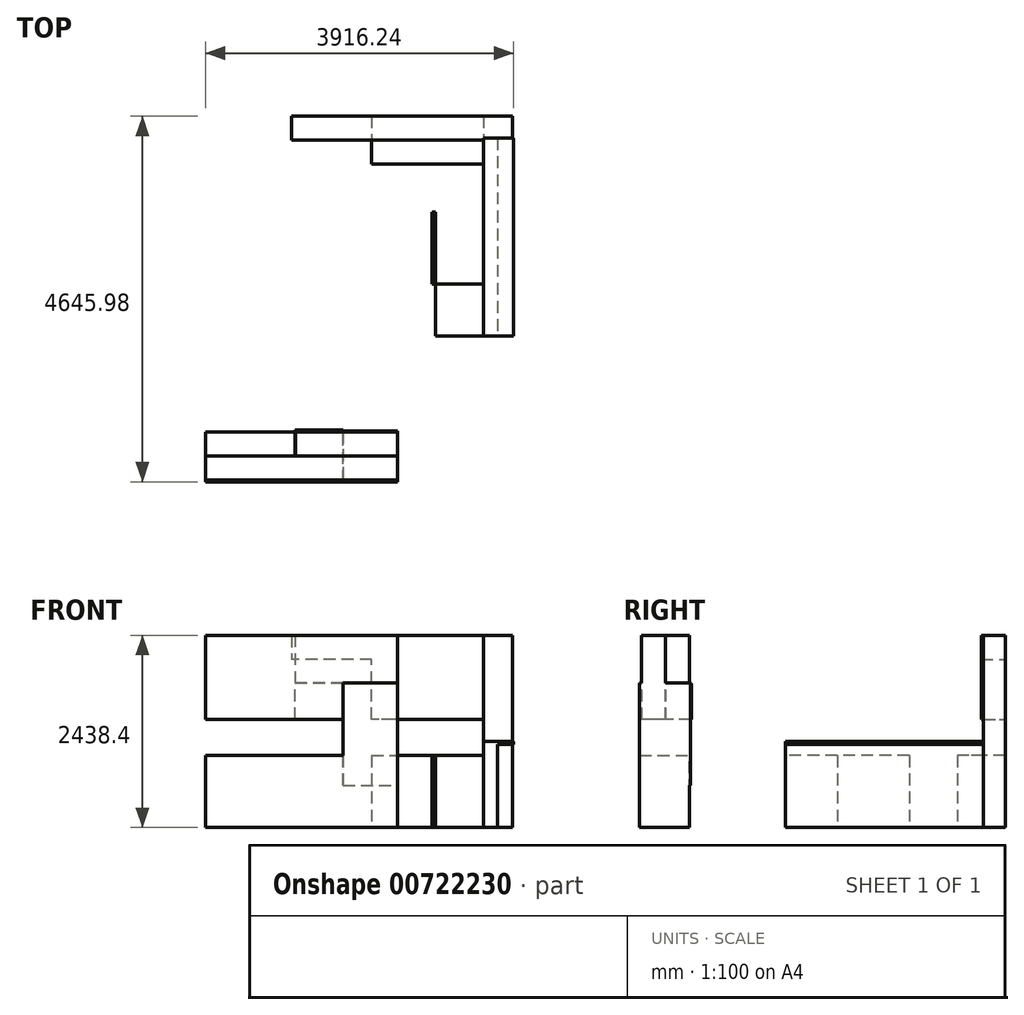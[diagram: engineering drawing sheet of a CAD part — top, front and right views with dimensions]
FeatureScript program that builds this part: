
annotation { "Feature Type Name" : "Feature", "Feature Type Description" : "" }
export const myFeature = defineFeature(function(context is Context, id is Id, definition is map)
    precondition{}
    {
        {
            var Q0;
            Q0=qCreatedBy(makeId("Top.planeOp"),FACE);
            var sketch = newSketch(context, id + "F0", { "sketchPlane" : qUnion([Q0])});
            skLineSegment(sketch, "E0.bottom", {"start": v(0, 0) * mm, "end": v(1422.4, 0) * mm});
            skLineSegment(sketch, "E0.top", {"start": v(0, -609.6) * mm, "end": v(1422.4, -609.6) * mm});
            skLineSegment(sketch, "E0.left", {"start": v(0, 0) * mm, "end": v(0, -609.6) * mm});
            skLineSegment(sketch, "E0.right", {"start": v(1422.4, 0) * mm, "end": v(1422.4, -609.6) * mm});
            skLineSegment(sketch, "E1.bottom", {"start": v(1422.4, -609.6) * mm, "end": v(812.8, -609.6) * mm});
            skLineSegment(sketch, "E1.top", {"start": v(1422.4, -2794) * mm, "end": v(812.8, -2794) * mm});
            skLineSegment(sketch, "E1.left", {"start": v(1422.4, -609.6) * mm, "end": v(1422.4, -2794) * mm});
            skLineSegment(sketch, "E1.right", {"start": v(812.8, -609.6) * mm, "end": v(812.8, -2794) * mm});
            skLineSegment(sketch, "E2.bottom", {"start": v(769.1, -1219.2) * mm, "end": v(1422.4, -1219.2) * mm});
            skLineSegment(sketch, "E2.top", {"start": v(769.1, -2133.6) * mm, "end": v(1422.4, -2133.6) * mm});
            skLineSegment(sketch, "E2.left", {"start": v(769.1, -1219.2) * mm, "end": v(769.1, -2133.6) * mm});
            skLineSegment(sketch, "E2.right", {"start": v(1422.4, -1219.2) * mm, "end": v(1422.4, -2133.6) * mm});
            skSolve(sketch);
        }
        {
            var Q0;
            Q0=makeQuery(id+"F0.imprint","IMPRINT",FACE,{"disambiguationData":[TD([[makeQuery(id+"F0.imprint","IMPRINT",EDGE,{"derivedFrom":sQuery(id+"F0.wireOp",EDGE,"E0.bottom")}),-1.0]])]});
            var Q1;
            {var subQ0=sQuery(id+"F0.wireOp",EDGE,"E1.bottom");Q1=makeQuery(id+"F0.imprint","IMPRINT",FACE,{"disambiguationData":[TD([[makeQuery(id+"F0.imprint","IMPRINT",EDGE,{"derivedFrom":subQ0}),1.0]])]});}
            var Q2;
            {var subQ5=sQuery(id+"F0.wireOp",EDGE,"E2.right");Q2=makeQuery(id+"F0.imprint","IMPRINT",FACE,{"disambiguationData":[TD([[makeQuery(id+"F0.imprint","IMPRINT",EDGE,{"derivedFrom":subQ5}),-1.0]])]});}
            var Q3;
            {var subQ5=sQuery(id+"F0.wireOp",EDGE,"E2.left");Q3=makeQuery(id+"F0.imprint","IMPRINT",FACE,{"disambiguationData":[TD([[makeQuery(id+"F0.imprint","IMPRINT",EDGE,{"derivedFrom":subQ5}),1.0]])]});}
            var Q4;
            {var subQ0=sQuery(id+"F0.wireOp",EDGE,"E1.top");Q4=makeQuery(id+"F0.imprint","IMPRINT",FACE,{"disambiguationData":[TD([[makeQuery(id+"F0.imprint","IMPRINT",EDGE,{"derivedFrom":subQ0}),-1.0]])]});}
            extrude(context, id + "F1", {"entities" : qUnion([Q0, Q1, Q2, Q3, Q4]), "depth" : 914.4 * mm, "offsetDistance" : 25.4 * mm});
        }
        {
            var Q0;
            Q0=makeQuery(id+"F1.opExtrude","SWEPT_FACE",FACE,{"disambiguationData":[OSD([sQuery(id+"F0.wireOp",EDGE,"E1.top")])]});
            var sketch = newSketch(context, id + "F2", { "sketchPlane" : qUnion([Q0])});
            skLineSegment(sketch, "E3.bottom", {"start": v(1422.4, 0) * mm, "end": v(1600.2, 0) * mm});
            skLineSegment(sketch, "E3.top", {"start": v(1422.4, 1092.2) * mm, "end": v(1600.2, 1092.2) * mm});
            skLineSegment(sketch, "E3.left", {"start": v(1422.4, 0) * mm, "end": v(1422.4, 1092.2) * mm});
            skLineSegment(sketch, "E3.right", {"start": v(1600.2, 0) * mm, "end": v(1600.2, 1092.2) * mm});
            skLineSegment(sketch, "E4.bottom", {"start": v(1600.2, 1092.2) * mm, "end": v(1803.4, 1092.2) * mm});
            skLineSegment(sketch, "E4.top", {"start": v(1600.2, 1054.1) * mm, "end": v(1803.4, 1054.1) * mm});
            skLineSegment(sketch, "E4.left", {"start": v(1600.2, 1092.2) * mm, "end": v(1600.2, 1054.1) * mm});
            skLineSegment(sketch, "E4.right", {"start": v(1803.4, 1092.2) * mm, "end": v(1803.4, 1054.1) * mm});
            skSolve(sketch);
        }
        {
            var Q0;
            {var subQ4=sQuery(id+"F2.wireOp",EDGE,"E3.bottom");Q0=makeQuery(id+"F2.imprint","IMPRINT",FACE,{"disambiguationData":[TD([[makeQuery(id+"F2.imprint","IMPRINT",EDGE,{"derivedFrom":subQ4}),1.0]])]});}
            var Q1;
            Q1=makeQuery(id+"F2.imprint","IMPRINT",FACE,{"disambiguationData":[TD([[makeQuery(id+"F2.imprint","IMPRINT",EDGE,{"derivedFrom":sQuery(id+"F2.wireOp",EDGE,"E4.bottom")}),-1.0]])]});
            extrude(context, id + "F3", {"entities" : qUnion([Q0, Q1]), "oppositeDirection" : true, "depth" : 2514.6 * mm, "offsetDistance" : 25.4 * mm});
        }
        {
            var Q0;
            Q0=makeQuery(id+"F1.opExtrude","CAP_FACE",FACE,{"disambiguationData":[OSD([sQuery(id+"F0.wireOp",EDGE,"E0.bottom"),sQuery(id+"F0.wireOp",EDGE,"E0.top"),sQuery(id+"F0.wireOp",EDGE,"E0.left"),sQuery(id+"F0.wireOp",EDGE,"E0.right"),sQuery(id+"F0.wireOp",EDGE,"E1.top"),sQuery(id+"F0.wireOp",EDGE,"E1.left"),sQuery(id+"F0.wireOp",EDGE,"E1.right"),sQuery(id+"F0.wireOp",EDGE,"E2.bottom"),sQuery(id+"F0.wireOp",EDGE,"E2.top"),sQuery(id+"F0.wireOp",EDGE,"E2.left"),sQuery(id+"F0.wireOp",EDGE,"E2.right")])],"isStart":true});
            var sketch = newSketch(context, id + "F4", { "sketchPlane" : qUnion([Q0])});
            skLineSegment(sketch, "E5.bottom", {"start": v(1422.4, 278.96) * mm, "end": v(1786.64, 278.96) * mm});
            skLineSegment(sketch, "E5.top", {"start": v(1422.4, 0) * mm, "end": v(1786.64, 0) * mm});
            skLineSegment(sketch, "E5.left", {"start": v(1422.4, 278.96) * mm, "end": v(1422.4, 0) * mm});
            skLineSegment(sketch, "E5.right", {"start": v(1786.64, 278.96) * mm, "end": v(1786.64, 0) * mm});
            skSolve(sketch);
        }
        {
            var Q0;
            Q0=makeQuery(id+"F4.imprint","IMPRINT",FACE,{"disambiguationData":[TD([[makeQuery(id+"F4.imprint","IMPRINT",EDGE,{"derivedFrom":sQuery(id+"F4.wireOp",EDGE,"E5.bottom")}),-1.0]])]});
            extrude(context, id + "F5", {"entities" : qUnion([Q0]), "operationType" : NewBodyOperationType.ADD, "oppositeDirection" : true, "depth" : 2438.4 * mm, "offsetDistance" : 25.4 * mm});
        }
        {
            var Q0;
            Q0=makeQuery(id+"F1.opExtrude","CAP_FACE",FACE,{"disambiguationData":[OSD([sQuery(id+"F0.wireOp",EDGE,"E0.bottom"),sQuery(id+"F0.wireOp",EDGE,"E0.top"),sQuery(id+"F0.wireOp",EDGE,"E0.left"),sQuery(id+"F0.wireOp",EDGE,"E0.right"),sQuery(id+"F0.wireOp",EDGE,"E1.top"),sQuery(id+"F0.wireOp",EDGE,"E1.left"),sQuery(id+"F0.wireOp",EDGE,"E1.right"),sQuery(id+"F0.wireOp",EDGE,"E2.bottom"),sQuery(id+"F0.wireOp",EDGE,"E2.top"),sQuery(id+"F0.wireOp",EDGE,"E2.left"),sQuery(id+"F0.wireOp",EDGE,"E2.right")])],"isStart":false});
            var sketch = newSketch(context, id + "F6", { "sketchPlane" : qUnion([Q0])});
            skLineSegment(sketch, "E6.bottom", {"start": v(921.5, -1270) * mm, "end": v(1320.8, -1270) * mm});
            skLineSegment(sketch, "E6.top", {"start": v(921.5, -2082.8) * mm, "end": v(1320.8, -2082.8) * mm});
            skLineSegment(sketch, "E6.left", {"start": v(870.7, -1320.8) * mm, "end": v(870.7, -2032) * mm});
            skLineSegment(sketch, "E6.right", {"start": v(1371.6, -1320.8) * mm, "end": v(1371.6, -2032) * mm});
            skPoint(sketch, "E7.visualSharp", {"position": v(870.7, -1270) * mm});
            skArc(sketch, "E7.filletArc", {"start": v(921.5, -1270) * mm, "mid": v(885.57, -1284.88) * mm, "end": v(870.7, -1320.8) * mm});
            skPoint(sketch, "E8.visualSharp", {"position": v(1371.6, -1270) * mm});
            skArc(sketch, "E8.filletArc", {"start": v(1371.6, -1320.8) * mm, "mid": v(1356.72, -1284.88) * mm, "end": v(1320.8, -1270) * mm});
            skPoint(sketch, "E9.visualSharp", {"position": v(1371.6, -2082.8) * mm});
            skArc(sketch, "E9.filletArc", {"start": v(1320.8, -2082.8) * mm, "mid": v(1356.72, -2067.92) * mm, "end": v(1371.6, -2032) * mm});
            skPoint(sketch, "E10.visualSharp", {"position": v(870.7, -2082.8) * mm});
            skArc(sketch, "E10.filletArc", {"start": v(870.7, -2032) * mm, "mid": v(885.57, -2067.92) * mm, "end": v(921.5, -2082.8) * mm});
            skSolve(sketch);
        }
        {
            var Q0;
            Q0=makeQuery(id+"F6.imprint","IMPRINT",FACE,{"disambiguationData":[TD([[makeQuery(id+"F6.imprint","IMPRINT",EDGE,{"derivedFrom":sQuery(id+"F6.wireOp",EDGE,"E6.bottom")}),-1.0]])]});
            extrude(context, id + "F7", {"entities" : qUnion([Q0]), "operationType" : NewBodyOperationType.REMOVE, "oppositeDirection" : true, "depth" : 203.2 * mm, "offsetDistance" : 25.4 * mm});
        }
        {
            var Q0;
            Q0=makeQuery(id+"F1.opExtrude","CAP_FACE",FACE,{"disambiguationData":[OSD([sQuery(id+"F0.wireOp",EDGE,"E0.bottom"),sQuery(id+"F0.wireOp",EDGE,"E0.top"),sQuery(id+"F0.wireOp",EDGE,"E0.left"),sQuery(id+"F0.wireOp",EDGE,"E0.right"),sQuery(id+"F0.wireOp",EDGE,"E1.top"),sQuery(id+"F0.wireOp",EDGE,"E1.left"),sQuery(id+"F0.wireOp",EDGE,"E1.right"),sQuery(id+"F0.wireOp",EDGE,"E2.bottom"),sQuery(id+"F0.wireOp",EDGE,"E2.top"),sQuery(id+"F0.wireOp",EDGE,"E2.left"),sQuery(id+"F0.wireOp",EDGE,"E2.right")])],"isStart":false});
            var sketch = newSketch(context, id + "F8", { "sketchPlane" : qUnion([Q0])});
            skLineSegment(sketch, "E11.bottom", {"start": v(325.56, -4010.98) * mm, "end": v(-2112.84, -4010.98) * mm});
            skLineSegment(sketch, "E11.top", {"start": v(325.56, -4620.58) * mm, "end": v(-2112.84, -4620.58) * mm});
            skLineSegment(sketch, "E11.left", {"start": v(325.56, -4010.98) * mm, "end": v(325.56, -4620.58) * mm});
            skLineSegment(sketch, "E11.right", {"start": v(-2112.84, -4010.98) * mm, "end": v(-2112.84, -4620.58) * mm});
            skSolve(sketch);
        }
        {
            var Q0;
            Q0=makeQuery(id+"F8.imprint","IMPRINT",FACE,{"disambiguationData":[TD([[makeQuery(id+"F8.imprint","IMPRINT",EDGE,{"derivedFrom":sQuery(id+"F8.wireOp",EDGE,"E11.bottom")}),1.0]])]});
            extrude(context, id + "F9", {"entities" : qUnion([Q0]), "oppositeDirection" : true, "depth" : 914.4 * mm, "offsetDistance" : 25.4 * mm});
        }
        {
            var Q0;
            Q0=makeQuery(id+"F5.boolean.opBoolean","MERGE",FACE,{"derivedFrom":[makeQuery(id+"F1.opExtrude","SWEPT_FACE",FACE,{"disambiguationData":[OSD([sQuery(id+"F0.wireOp",EDGE,"E0.bottom")])]}),makeQuery(id+"F5.opExtrude","SWEPT_FACE",FACE,{"disambiguationData":[OSD([sQuery(id+"F4.wireOp",EDGE,"E5.top")])]})]});
            var sketch = newSketch(context, id + "F10", { "sketchPlane" : qUnion([Q0])});
            skLineSegment(sketch, "E12.bottom", {"start": v(-1422.4, 1371.6) * mm, "end": v(0, 1371.6) * mm});
            skLineSegment(sketch, "E12.top", {"start": v(-1422.4, 2438.4) * mm, "end": v(0, 2438.4) * mm});
            skLineSegment(sketch, "E12.left", {"start": v(-1422.4, 1371.6) * mm, "end": v(-1422.4, 2438.4) * mm});
            skLineSegment(sketch, "E12.right", {"start": v(0, 1371.6) * mm, "end": v(0, 2438.4) * mm});
            skLineSegment(sketch, "E13.bottom", {"start": v(0, 2438.4) * mm, "end": v(1016, 2438.4) * mm});
            skLineSegment(sketch, "E13.top", {"start": v(0, 2133.6) * mm, "end": v(1016, 2133.6) * mm});
            skLineSegment(sketch, "E13.left", {"start": v(0, 2438.4) * mm, "end": v(0, 2133.6) * mm});
            skLineSegment(sketch, "E13.right", {"start": v(1016, 2438.4) * mm, "end": v(1016, 2133.6) * mm});
            skSolve(sketch);
        }
        {
            var Q0;
            Q0=makeQuery(id+"F10.imprint","IMPRINT",FACE,{"disambiguationData":[TD([[makeQuery(id+"F10.imprint","IMPRINT",EDGE,{"derivedFrom":sQuery(id+"F10.wireOp",EDGE,"E12.bottom")}),1.0]])]});
            var Q1;
            Q1=makeQuery(id+"F10.imprint","IMPRINT",FACE,{"disambiguationData":[TD([[makeQuery(id+"F10.imprint","IMPRINT",EDGE,{"derivedFrom":sQuery(id+"F10.wireOp",EDGE,"E13.bottom")}),-1.0]])]});
            extrude(context, id + "F11", {"entities" : qUnion([Q0, Q1]), "operationType" : NewBodyOperationType.ADD, "oppositeDirection" : true, "depth" : 304.8 * mm, "offsetDistance" : 25.4 * mm});
        }
        {
            var Q0;
            Q0=makeQuery(id+"F9.opExtrude","SWEPT_FACE",FACE,{"disambiguationData":[OSD([sQuery(id+"F8.wireOp",EDGE,"E11.top")])]});
            var sketch = newSketch(context, id + "F12", { "sketchPlane" : qUnion([Q0])});
            skLineSegment(sketch, "E14.bottom", {"start": v(325.56, 533.4) * mm, "end": v(-363.42, 533.4) * mm});
            skLineSegment(sketch, "E14.top", {"start": v(325.56, 1831.97) * mm, "end": v(-363.42, 1831.97) * mm});
            skLineSegment(sketch, "E14.left", {"start": v(325.56, 533.4) * mm, "end": v(325.56, 1831.98) * mm});
            skLineSegment(sketch, "E14.right", {"start": v(-363.42, 533.4) * mm, "end": v(-363.42, 1831.97) * mm});
            skSolve(sketch);
        }
        {
            var Q0;
            {var subQ0=sQuery(id+"F12.wireOp",EDGE,"E14.top");Q0=makeQuery(id+"F12.imprint","IMPRINT",FACE,{"disambiguationData":[TD([[makeQuery(id+"F12.imprint","IMPRINT",EDGE,{"derivedFrom":subQ0}),1.0]])]});}
            var Q1;
            {var subQ0=sQuery(id+"F12.wireOp",EDGE,"E14.bottom");Q1=makeQuery(id+"F12.imprint","IMPRINT",FACE,{"disambiguationData":[TD([[makeQuery(id+"F12.imprint","IMPRINT",EDGE,{"derivedFrom":subQ0}),-1.0]])]});}
            extrude(context, id + "F13", {"entities" : qUnion([Q0, Q1]), "operationType" : NewBodyOperationType.ADD, "oppositeDirection" : true, "depth" : 622.3 * mm, "offsetDistance" : 25.4 * mm});
        }
        {
            var Q0;
            Q0=makeQuery(id+"F13.boolean.opBoolean","MERGE",FACE,{"derivedFrom":[makeQuery(id+"F9.opExtrude","SWEPT_FACE",FACE,{"disambiguationData":[OSD([sQuery(id+"F8.wireOp",EDGE,"E11.top")])]}),makeQuery(id+"F13.opExtrude","CAP_FACE",FACE,{"disambiguationData":[OSD([sQuery(id+"F12.wireOp",EDGE,"E14.bottom"),sQuery(id+"F12.wireOp",EDGE,"E14.top"),sQuery(id+"F12.wireOp",EDGE,"E14.left"),sQuery(id+"F12.wireOp",EDGE,"E14.right")])],"isStart":true})]});
            var sketch = newSketch(context, id + "F14", { "sketchPlane" : qUnion([Q0])});
            skLineSegment(sketch, "E15.bottom", {"start": v(325.56, 1831.97) * mm, "end": v(-363.42, 1831.97) * mm});
            skLineSegment(sketch, "E15.top", {"start": v(325.56, 2438.4) * mm, "end": v(-363.42, 2438.4) * mm});
            skLineSegment(sketch, "E15.left", {"start": v(325.56, 1831.97) * mm, "end": v(325.56, 2438.4) * mm});
            skLineSegment(sketch, "E15.right", {"start": v(-363.42, 1831.97) * mm, "end": v(-363.42, 2438.4) * mm});
            skLineSegment(sketch, "E16.bottom", {"start": v(-363.42, 2438.4) * mm, "end": v(-2112.84, 2438.4) * mm});
            skLineSegment(sketch, "E16.top", {"start": v(-363.42, 1371.6) * mm, "end": v(-2112.84, 1371.6) * mm});
            skLineSegment(sketch, "E16.left", {"start": v(-363.42, 2438.4) * mm, "end": v(-363.42, 1371.6) * mm});
            skLineSegment(sketch, "E16.right", {"start": v(-2112.84, 2438.4) * mm, "end": v(-2112.84, 1371.6) * mm});
            skSolve(sketch);
        }
        {
            var Q0;
            {var subQ3=sQuery(id+"F14.wireOp",EDGE,"E16.bottom");Q0=makeQuery(id+"F14.imprint","IMPRINT",FACE,{"disambiguationData":[TD([[makeQuery(id+"F14.imprint","IMPRINT",EDGE,{"derivedFrom":subQ3}),1.0]])]});}
            var Q1;
            {var subQ0=sQuery(id+"F14.wireOp",EDGE,"E15.bottom");Q1=makeQuery(id+"F14.imprint","IMPRINT",FACE,{"disambiguationData":[TD([[makeQuery(id+"F14.imprint","IMPRINT",EDGE,{"derivedFrom":subQ0}),-1.0]])]});}
            extrude(context, id + "F15", {"entities" : qUnion([Q0, Q1]), "oppositeDirection" : true, "depth" : 304.8 * mm, "offsetDistance" : 25.4 * mm});
        }
        {
            var Q0;
            Q0=makeQuery(id+"F15.opExtrude","CAP_FACE",FACE,{"disambiguationData":[OSD([sQuery(id+"F14.wireOp",EDGE,"E15.bottom"),sQuery(id+"F14.wireOp",EDGE,"E15.top"),sQuery(id+"F14.wireOp",EDGE,"E15.left"),sQuery(id+"F14.wireOp",EDGE,"E16.bottom"),sQuery(id+"F14.wireOp",EDGE,"E16.top"),sQuery(id+"F14.wireOp",EDGE,"E16.left"),sQuery(id+"F14.wireOp",EDGE,"E16.right")])],"isStart":true});
            var sketch = newSketch(context, id + "F16", { "sketchPlane" : qUnion([Q0])});
            skLineSegment(sketch, "E17.bottom", {"start": v(-363.42, 1371.6) * mm, "end": v(-973.02, 1371.6) * mm});
            skLineSegment(sketch, "E17.top", {"start": v(-363.42, 1828.8) * mm, "end": v(-973.02, 1828.8) * mm});
            skLineSegment(sketch, "E17.left", {"start": v(-363.42, 1371.6) * mm, "end": v(-363.42, 1828.8) * mm});
            skLineSegment(sketch, "E17.right", {"start": v(-973.02, 1371.6) * mm, "end": v(-973.02, 1828.8) * mm});
            skSolve(sketch);
        }
        {
            var Q0;
            Q0=makeQuery(id+"F16.imprint","IMPRINT",FACE,{"disambiguationData":[TD([[makeQuery(id+"F16.imprint","IMPRINT",EDGE,{"derivedFrom":sQuery(id+"F16.wireOp",EDGE,"E17.bottom")}),-1.0]])]});
            extrude(context, id + "F17", {"entities" : qUnion([Q0]), "oppositeDirection" : true, "depth" : 635 * mm, "offsetDistance" : 25.4 * mm});
        }
        {
            var Q0;
            Q0=makeQuery(id+"F15.opExtrude","CAP_FACE",FACE,{"disambiguationData":[OSD([sQuery(id+"F14.wireOp",EDGE,"E15.bottom"),sQuery(id+"F14.wireOp",EDGE,"E15.top"),sQuery(id+"F14.wireOp",EDGE,"E15.left"),sQuery(id+"F14.wireOp",EDGE,"E16.bottom"),sQuery(id+"F14.wireOp",EDGE,"E16.top"),sQuery(id+"F14.wireOp",EDGE,"E16.left"),sQuery(id+"F14.wireOp",EDGE,"E16.right")])],"isStart":false});
            var sketch = newSketch(context, id + "F18", { "sketchPlane" : qUnion([Q0])});
            skLineSegment(sketch, "E18.bottom", {"start": v(-325.56, 1831.97) * mm, "end": v(967.67, 1831.97) * mm});
            skLineSegment(sketch, "E18.top", {"start": v(-325.56, 2438.4) * mm, "end": v(967.67, 2438.4) * mm});
            skLineSegment(sketch, "E18.left", {"start": v(-325.56, 1831.97) * mm, "end": v(-325.56, 2438.4) * mm});
            skLineSegment(sketch, "E18.right", {"start": v(967.67, 1831.97) * mm, "end": v(967.67, 2438.4) * mm});
            skSolve(sketch);
        }
        {
            var Q0;
            Q0=makeQuery(id+"F18.imprint","IMPRINT",FACE,{"disambiguationData":[TD([[makeQuery(id+"F18.imprint","IMPRINT",EDGE,{"derivedFrom":sQuery(id+"F18.wireOp",EDGE,"E18.top")}),-1.0]])]});
            extrude(context, id + "F19", {"entities" : qUnion([Q0]), "depth" : 304.8 * mm, "offsetDistance" : 25.4 * mm});
        }
        {
            var Q0;
            Q0=makeQuery(id+"F13.boolean.opBoolean","MERGE",FACE,{"derivedFrom":[makeQuery(id+"F9.opExtrude","SWEPT_FACE",FACE,{"disambiguationData":[OSD([sQuery(id+"F8.wireOp",EDGE,"E11.top")])]}),makeQuery(id+"F13.opExtrude","CAP_FACE",FACE,{"disambiguationData":[OSD([sQuery(id+"F12.wireOp",EDGE,"E14.bottom"),sQuery(id+"F12.wireOp",EDGE,"E14.top"),sQuery(id+"F12.wireOp",EDGE,"E14.left"),sQuery(id+"F12.wireOp",EDGE,"E14.right")])],"isStart":true})]});
            extrude(context, id + "F20", {"entities" : qUnion([Q0]), "operationType" : NewBodyOperationType.ADD, "depth" : 25.4 * mm, "offsetDistance" : 25.4 * mm});
        }
    });
